# Revit family: Thorn VOYAGER ONE
name_source: partatom
category: Lighting Fixtures
revit_build: Autodesk Revit 2016 (Build: 20150220_1215(x64)
units: mm (PartAtom-declared; Revit-internal decimal feet)

## family parameters
Cut with Voids When Loaded = No
Host = Face
Light Source = Yes
OmniClass Number = 23.80.70.11
OmniClass Title = Luminaries for Internal Lighting
Part Type = Normal
Room Calculation Point = No
Round Connector Dimension = Use Diameter
Shared = No

## types (1)
- MS ANT E3 WH IP65
    Apparent Load = 4 VA
    Assembly Code = D5020200
    Body = ZG_Metal_White
    Color Filter = 16777215
    Cover = ZG_PMMA
    Default Elevation = 0 mm  [stored 0 ft]
    Description = LED emergency lighting luminaire
    Dimming Lamp Color Temperature Shift = <None>
    Emit Shape Visible in Rendering = No
    Emit from Rectangle Length = 59 mm
    Emit from Rectangle Width = 303 mm  [stored 0.994094 ft]
    Height = 59 mm
    Lamp = LED
    Length = 336 mm  [stored 1.10236 ft]
    Manufacturer = Thorn Lighting
    Model = 96631596
    Photometric Web File = 96631596_(STD).IES
    Tilt Angle = -90.00°
    URL = www.thornlighting.com/96631596
    Voltage = 230 V
    Width = 54 mm

note: [stored X ft] marks values corroborated as IEEE doubles in the binary element streams (Revit-internal decimal feet)

## geometry (parser evidence)
native form markers: Sweep x2
no freeform markers — native parametric forms only
